# Revit family: 3PD-LAYIN-ROUND NECK
name_source: partatom
category: Air Terminals
revit_build: Autodesk Revit 2018 (Build: 20170223_1515(x64)
units: mm (PartAtom-declared; Revit-internal decimal feet)

## family parameters
Always vertical = Yes
Cut with Voids When Loaded = No
OmniClass Number = 23.75.00.00
OmniClass Title = Climate Control (HVAC)
Part Type = Normal
Room Calculation Point = No
Round Connector Dimension = Use Diameter
Shared = No
Work Plane-Based = No

## types (20) — shared parameters
Basedim = 1' - 11 3/4"
Basethickness = 0' - 0 1/32"
BotRad = 0' - 0 3/8"
Botdim = 1' - 10 15/32"
CollarHi = 0' - 1 1/2"
Description = Perforated Ceiling Return/Exhaust; Ducted 24x24 Module Size
FirstLevel = 0' - 0 9/16"
Manufacturer = ANEMOSTAT PRODUCTS
Middim = 1' - 9 7/32"
Model = 3PD
SecondLevel = 0' - 1 1/2"
TopRad = 0' - 0 29/32"
Topdim = 1' - 6 13/16"
URL = https://www.anemostat-hvac.com
Wall23 = 1' - 11"

## per-type parameters (varying)
| type | Material | Neck Size | Round Collar | Square Collar |
| 3PD-L, 18" DIA, ALUM | Aluminum | 1' - 6" | 1' - 5 7/8" | 1' - 5 3/4" |
| 3PD-L, 18" DIA, STEEL | STEEL | 1' - 6" | 1' - 5 7/8" | 1' - 5 3/4" |
| 3PD-L, 16" DIA, STEEL | STEEL | 1' - 4" | 1' - 3 7/8" | 1' - 3 3/4" |
| 3PD-L, 14" DIA, STEEL | STEEL | 1' - 2" | 1' - 1 7/8" | 1' - 1 3/4" |
| 3PD-L, 12" DIA, STEEL | STEEL | 1' - 0" | 0' - 11 7/8" | 0' - 11 3/4" |
| 3PD-L, 10" DIA, STEEL | STEEL | 0' - 10" | 0' - 9 7/8" | 0' - 9 3/4" |
| 3PD-L, 09" DIA, STEEL | STEEL | 0' - 9" | 0' - 8 7/8" | 0' - 8 3/4" |
| 3PD-L, 08" DIA, STEEL | STEEL | 0' - 8" | 0' - 7 7/8" | 0' - 7 3/4" |
| 3PD-L, 07" DIA, STEEL | STEEL | 0' - 7" | 0' - 6 7/8" | 0' - 6 3/4" |
| 3PD-L, 06" DIA, STEEL | STEEL | 0' - 6" | 0' - 5 7/8" | 0' - 5 3/4" |
| 3PD-L, 05" DIA, STEEL | STEEL | 0' - 5" | 0' - 4 7/8" | 0' - 4 3/4" |
| 3PD-L, 05" DIA, ALUM | Aluminum | 0' - 5" | 0' - 4 7/8" | 0' - 4 3/4" |
| 3PD-L, 06" DIA, ALUM | Aluminum | 0' - 6" | 0' - 5 7/8" | 0' - 5 3/4" |
| 3PD-L, 07" DIA, ALUM | Aluminum | 0' - 7" | 0' - 6 7/8" | 0' - 6 3/4" |
| 3PD-L, 08" DIA, ALUM | Aluminum | 0' - 8" | 0' - 7 7/8" | 0' - 7 3/4" |
| 3PD-L, 09" DIA, ALUM | Aluminum | 0' - 9" | 0' - 8 7/8" | 0' - 8 3/4" |
| 3PD-L, 10" DIA, ALUM | Aluminum | 0' - 10" | 0' - 9 7/8" | 0' - 9 3/4" |
| 3PD-L, 12" DIA, ALUM | Aluminum | 1' - 0" | 0' - 11 7/8" | 0' - 11 3/4" |
| 3PD-L, 14" DIA, ALUM | Aluminum | 1' - 2" | 1' - 1 7/8" | 1' - 1 3/4" |
| 3PD-L, 16" DIA, ALUM | Aluminum | 1' - 4" | 1' - 3 7/8" | 1' - 3 3/4" |

## geometry (parser evidence)
native form markers: Sweep x3
no freeform markers — native parametric forms only
